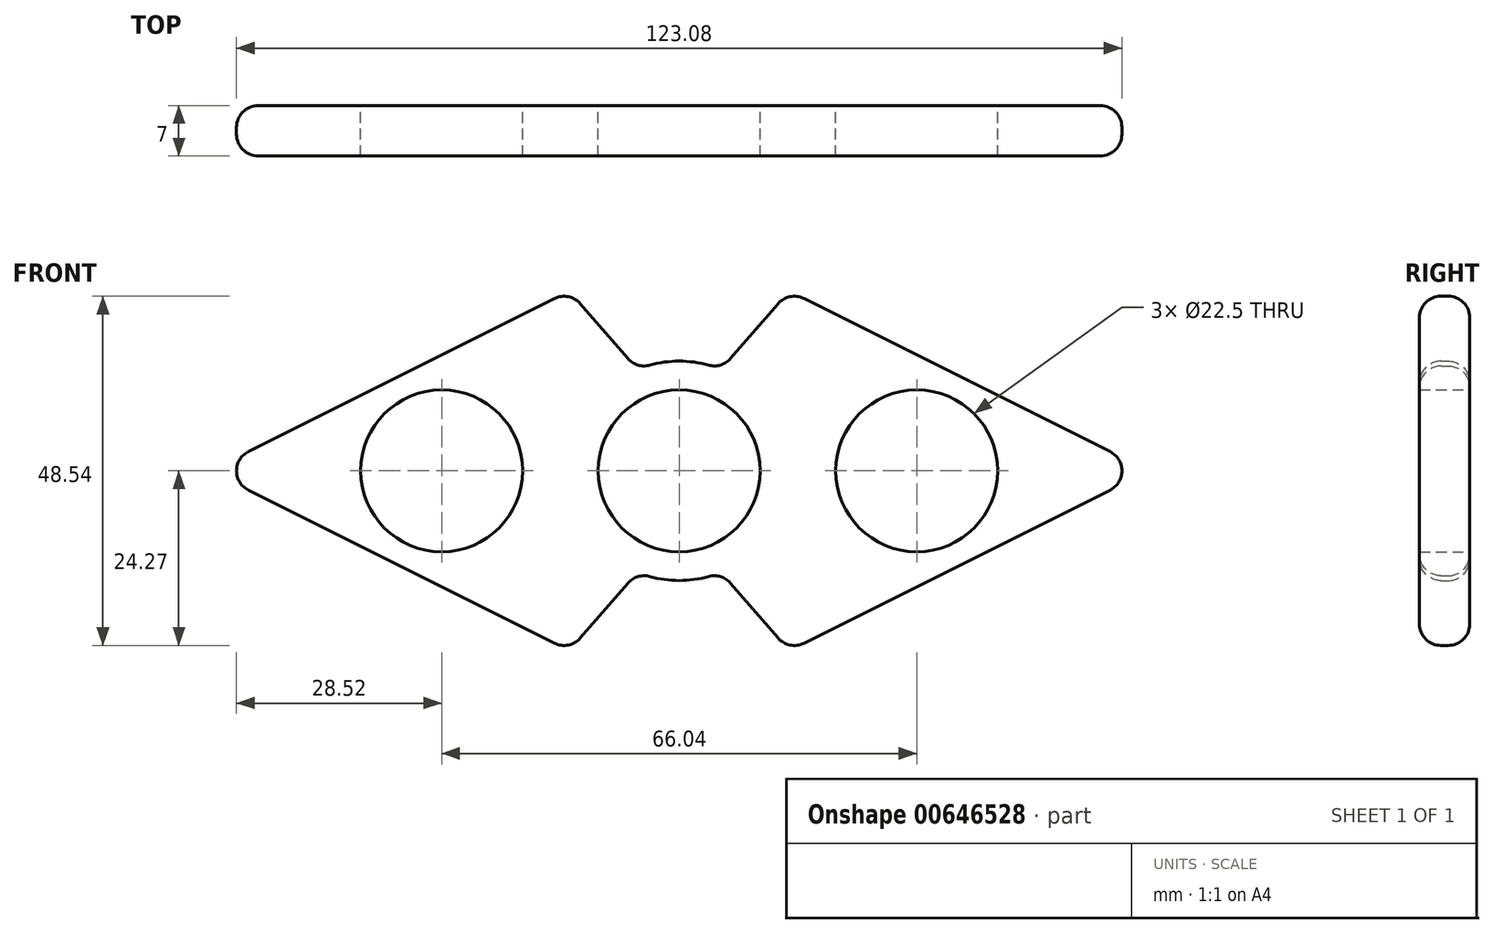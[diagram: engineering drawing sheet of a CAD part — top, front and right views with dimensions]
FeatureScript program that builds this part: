
annotation { "Feature Type Name" : "Feature", "Feature Type Description" : "" }
export const myFeature = defineFeature(function(context is Context, id is Id, definition is map)
    precondition{}
    {
        {
            var Q0;
            Q0=qCreatedBy(makeId("Front.planeOp"),FACE);
            var sketch = newSketch(context, id + "F0", { "sketchPlane" : qUnion([Q0])});
            skCircle(sketch, "E0", {"center": v(0, 0) * mm, "radius": 11.25 * mm});
            skCircle(sketch, "E1.0", {"center": v(0, 0) * mm, "radius": 15.25 * mm});
            skLineSegment(sketch, "E2", {"start": v(15.25, 0) * mm, "end": v(15.25, 25) * mm});
            skLineSegment(sketch, "E3", {"start": v(15.25, 25) * mm, "end": v(65.25, 0) * mm});
            skLineSegment(sketch, "E4", {"start": v(15.25, 0) * mm, "end": v(15.25, -25) * mm});
            skLineSegment(sketch, "E5", {"start": v(15.25, -25) * mm, "end": v(65.25, 0) * mm});
            skLineSegment(sketch, "E6", {"start": v(0, 0) * mm, "end": v(0, -15.25) * mm, "construction": true});
            skLineSegment(sketch, "E7.1.0", {"start": v(0, 0) * mm, "end": v(5.84, -14.09) * mm, "construction": true});
            skLineSegment(sketch, "E7.2.0", {"start": v(0, 0) * mm, "end": v(10.78, -10.78) * mm, "construction": true});
            skLineSegment(sketch, "E7.3.0", {"start": v(0, 0) * mm, "end": v(14.09, -5.84) * mm, "construction": true});
            skLineSegment(sketch, "E7.4.0", {"start": v(0, 0) * mm, "end": v(15.25, 0) * mm, "construction": true});
            skLineSegment(sketch, "E7.5.0", {"start": v(0, 0) * mm, "end": v(14.09, 5.84) * mm, "construction": true});
            skLineSegment(sketch, "E7.6.0", {"start": v(0, 0) * mm, "end": v(10.78, 10.78) * mm, "construction": true});
            skLineSegment(sketch, "E7.7.0", {"start": v(0, 0) * mm, "end": v(5.84, 14.09) * mm, "construction": true});
            skLineSegment(sketch, "E8.2.8.0", {"start": v(0, 0) * mm, "end": v(0, 15.25) * mm, "construction": true});
            skLineSegment(sketch, "E8.2.9.0", {"start": v(0, 0) * mm, "end": v(-5.84, 14.09) * mm, "construction": true});
            skLineSegment(sketch, "E8.2.10.0", {"start": v(0, 0) * mm, "end": v(-10.78, 10.78) * mm, "construction": true});
            skLineSegment(sketch, "E8.2.11.0", {"start": v(0, 0) * mm, "end": v(-14.09, 5.84) * mm, "construction": true});
            skLineSegment(sketch, "E8.2.12.0", {"start": v(0, 0) * mm, "end": v(-15.25, 0) * mm, "construction": true});
            skLineSegment(sketch, "E8.2.13.0", {"start": v(0, 0) * mm, "end": v(-14.09, -5.84) * mm, "construction": true});
            skLineSegment(sketch, "E8.2.14.0", {"start": v(0, 0) * mm, "end": v(-10.78, -10.78) * mm, "construction": true});
            skLineSegment(sketch, "E8.2.15.0", {"start": v(0, 0) * mm, "end": v(-5.84, -14.09) * mm, "construction": true});
            skLineSegment(sketch, "E9.1.0", {"start": v(-15.25, -25) * mm, "end": v(-65.25, 0) * mm});
            skLineSegment(sketch, "E9.1.1", {"start": v(-15.25, 0) * mm, "end": v(-15.25, 25) * mm});
            skLineSegment(sketch, "E9.1.2", {"start": v(-15.25, 25) * mm, "end": v(-65.25, 0) * mm});
            skLineSegment(sketch, "E9.1.3", {"start": v(-15.25, 0) * mm, "end": v(-15.25, -25) * mm});
            skLineSegment(sketch, "E10", {"start": v(-5.84, -14.09) * mm, "end": v(-15.25, -25) * mm});
            skLineSegment(sketch, "E11", {"start": v(15.25, -25) * mm, "end": v(5.84, -14.09) * mm});
            skLineSegment(sketch, "E12", {"start": v(15.25, 25) * mm, "end": v(5.84, 14.09) * mm});
            skLineSegment(sketch, "E13", {"start": v(-15.25, 25) * mm, "end": v(-5.84, 14.09) * mm});
            skCircle(sketch, "E14", {"center": v(-33.02, 0) * mm, "radius": 11.25 * mm});
            skCircle(sketch, "E15", {"center": v(33.02, 0) * mm, "radius": 11.25 * mm});
            skSolve(sketch);
        }
        {
            var Q0;
            Q0 = qSketchRegion(id + "F0", true);
            extrude(context, id + "F1", {"entities" : qUnion([Q0]), "depth" : 7 * mm, "offsetDistance" : 25.4 * mm});
        }
        {
            var Q0;
            Q0=makeQuery(id+"F1.opExtrude","SWEPT_FACE",FACE,{"disambiguationData":[OSD([sQuery(id+"F0.wireOp",EDGE,"E10")])]});
            var Q1;
            {var subQ0=sQuery(id+"F0.wireOp",EDGE,"E1.0");Q1=makeQuery(id+"F1.opExtrude","SWEPT_FACE",FACE,{"disambiguationData":[OSD([subQ0]),TDD([makeQuery(id+"F0.imprint","IMPRINT",EDGE,{"disambiguationData":[TD([[makeQuery(id+"F0.imprint","INTERSECT",VERTEX,{"derivedFrom":[subQ0,sQuery(id+"F0.wireOp",EDGE,"E10")]}),-1.0]])],"derivedFrom":subQ0})])]});}
            var Q2;
            Q2=makeQuery(id+"F1.opExtrude","SWEPT_FACE",FACE,{"disambiguationData":[OSD([sQuery(id+"F0.wireOp",EDGE,"E11")])]});
            var Q3;
            Q3=makeQuery(id+"F1.opExtrude","SWEPT_FACE",FACE,{"disambiguationData":[OSD([sQuery(id+"F0.wireOp",EDGE,"E9.1.0")])]});
            var Q4;
            Q4=makeQuery(id+"F1.opExtrude","SWEPT_FACE",FACE,{"disambiguationData":[OSD([sQuery(id+"F0.wireOp",EDGE,"E5")])]});
            var Q5;
            Q5=makeQuery(id+"F1.opExtrude","SWEPT_FACE",FACE,{"disambiguationData":[OSD([sQuery(id+"F0.wireOp",EDGE,"E3")])]});
            var Q6;
            Q6=makeQuery(id+"F1.opExtrude","SWEPT_FACE",FACE,{"disambiguationData":[OSD([sQuery(id+"F0.wireOp",EDGE,"E12")])]});
            var Q7;
            {var subQ0=sQuery(id+"F0.wireOp",EDGE,"E1.0");Q7=makeQuery(id+"F1.opExtrude","SWEPT_FACE",FACE,{"disambiguationData":[OSD([subQ0]),TDD([makeQuery(id+"F0.imprint","IMPRINT",EDGE,{"disambiguationData":[TD([[makeQuery(id+"F0.imprint","INTERSECT",VERTEX,{"derivedFrom":[subQ0,sQuery(id+"F0.wireOp",EDGE,"E12")]}),-1.0]])],"derivedFrom":subQ0})])]});}
            var Q8;
            Q8=makeQuery(id+"F1.opExtrude","SWEPT_FACE",FACE,{"disambiguationData":[OSD([sQuery(id+"F0.wireOp",EDGE,"E13")])]});
            var Q9;
            Q9=makeQuery(id+"F1.opExtrude","SWEPT_FACE",FACE,{"disambiguationData":[OSD([sQuery(id+"F0.wireOp",EDGE,"E9.1.2")])]});
            fillet(context, id + "F2", {"entities" : qUnion([Q0, Q1, Q2, Q3, Q4, Q5, Q6, Q7, Q8, Q9]), "radius" : 3 * mm, "tangentPropagation" : true, "allowEdgeOverflow" : false});
        }
    });
